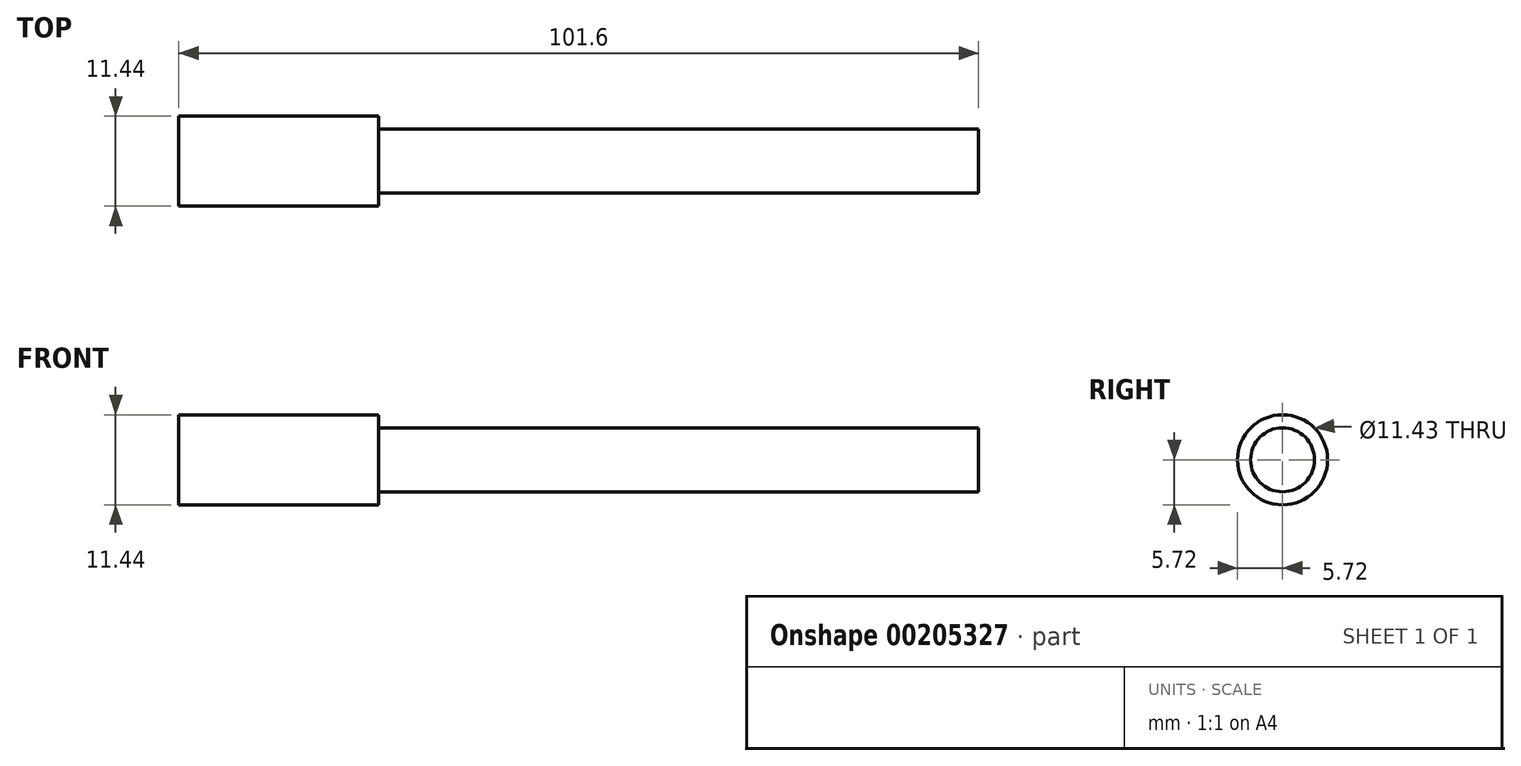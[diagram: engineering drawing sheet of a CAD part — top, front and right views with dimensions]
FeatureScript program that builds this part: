
annotation { "Feature Type Name" : "Feature", "Feature Type Description" : "" }
export const myFeature = defineFeature(function(context is Context, id is Id, definition is map)
    precondition{}
    {
        {
            var Q0;
            Q0=qCreatedBy(makeId("Right.planeOp"),FACE);
            var sketch = newSketch(context, id + "F0", { "sketchPlane" : qUnion([Q0])});
            skCircle(sketch, "E0", {"center": v(0, 0) * mm, "radius": 4.06 * mm});
            skSolve(sketch);
        }
        {
            var Q0;
            Q0=sQuery(id+"F0.wireOp",EDGE,"E0");
            extrude(context, id + "F1", {"bodyType" : ToolBodyType.SURFACE, "surfaceEntities" : qUnion([Q0]), "depth" : 76.2 * mm});
        }
        {
            var Q0;
            Q0=qCreatedBy(makeId("Right.planeOp"),FACE);
            var sketch = newSketch(context, id + "F2", { "sketchPlane" : qUnion([Q0])});
            skCircle(sketch, "E1", {"center": v(0, 0) * mm, "radius": 5.72 * mm});
            skSolve(sketch);
        }
        {
            var Q0;
            Q0=sQuery(id+"F2.wireOp",EDGE,"E1");
            extrude(context, id + "F3", {"bodyType" : ToolBodyType.SURFACE, "operationType" : NewBodyOperationType.REMOVE, "surfaceEntities" : qUnion([Q0]), "oppositeDirection" : true, "depth" : 25.4 * mm});
        }
    });
